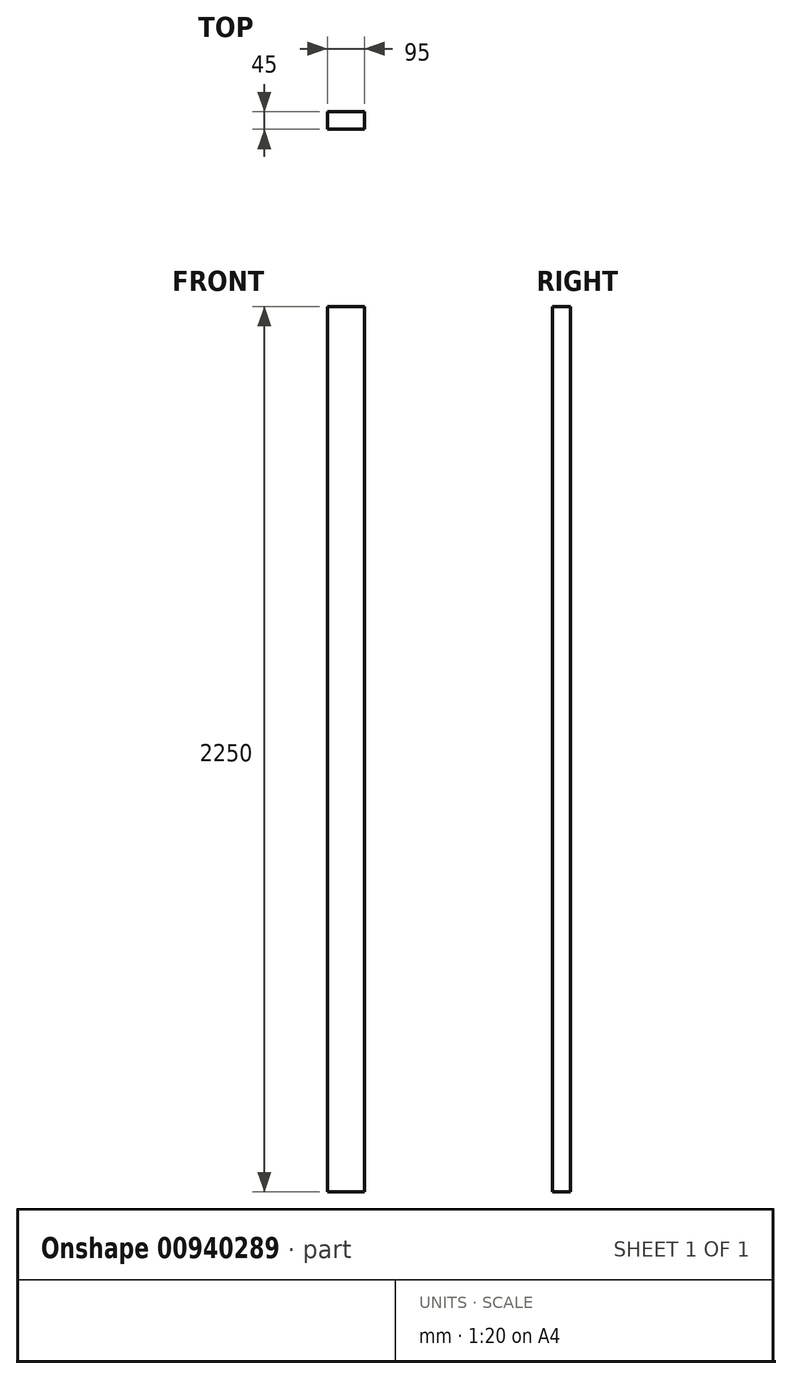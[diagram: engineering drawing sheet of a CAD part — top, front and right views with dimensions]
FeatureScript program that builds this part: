
annotation { "Feature Type Name" : "Feature", "Feature Type Description" : "" }
export const myFeature = defineFeature(function(context is Context, id is Id, definition is map)
    precondition{}
    {
        {
            var Q0;
            Q0=qCreatedBy(makeId("Top.planeOp"),FACE);
            var sketch = newSketch(context, id + "F0", { "sketchPlane" : qUnion([Q0])});
            skLineSegment(sketch, "E0.bottom", {"start": v(-47.5, 22.5) * mm, "end": v(47.5, 22.5) * mm});
            skLineSegment(sketch, "E0.top", {"start": v(-47.5, -22.5) * mm, "end": v(47.5, -22.5) * mm});
            skLineSegment(sketch, "E0.left", {"start": v(-47.5, 22.5) * mm, "end": v(-47.5, -22.5) * mm});
            skLineSegment(sketch, "E0.right", {"start": v(47.5, 22.5) * mm, "end": v(47.5, -22.5) * mm});
            skSolve(sketch);
        }
        {
            var Q0;
            Q0 = qSketchRegion(id + "F0", true);
            extrude(context, id + "F1", {"entities" : qUnion([Q0]), "depth" : 2250 * mm, "offsetDistance" : 25 * mm});
        }
    });
